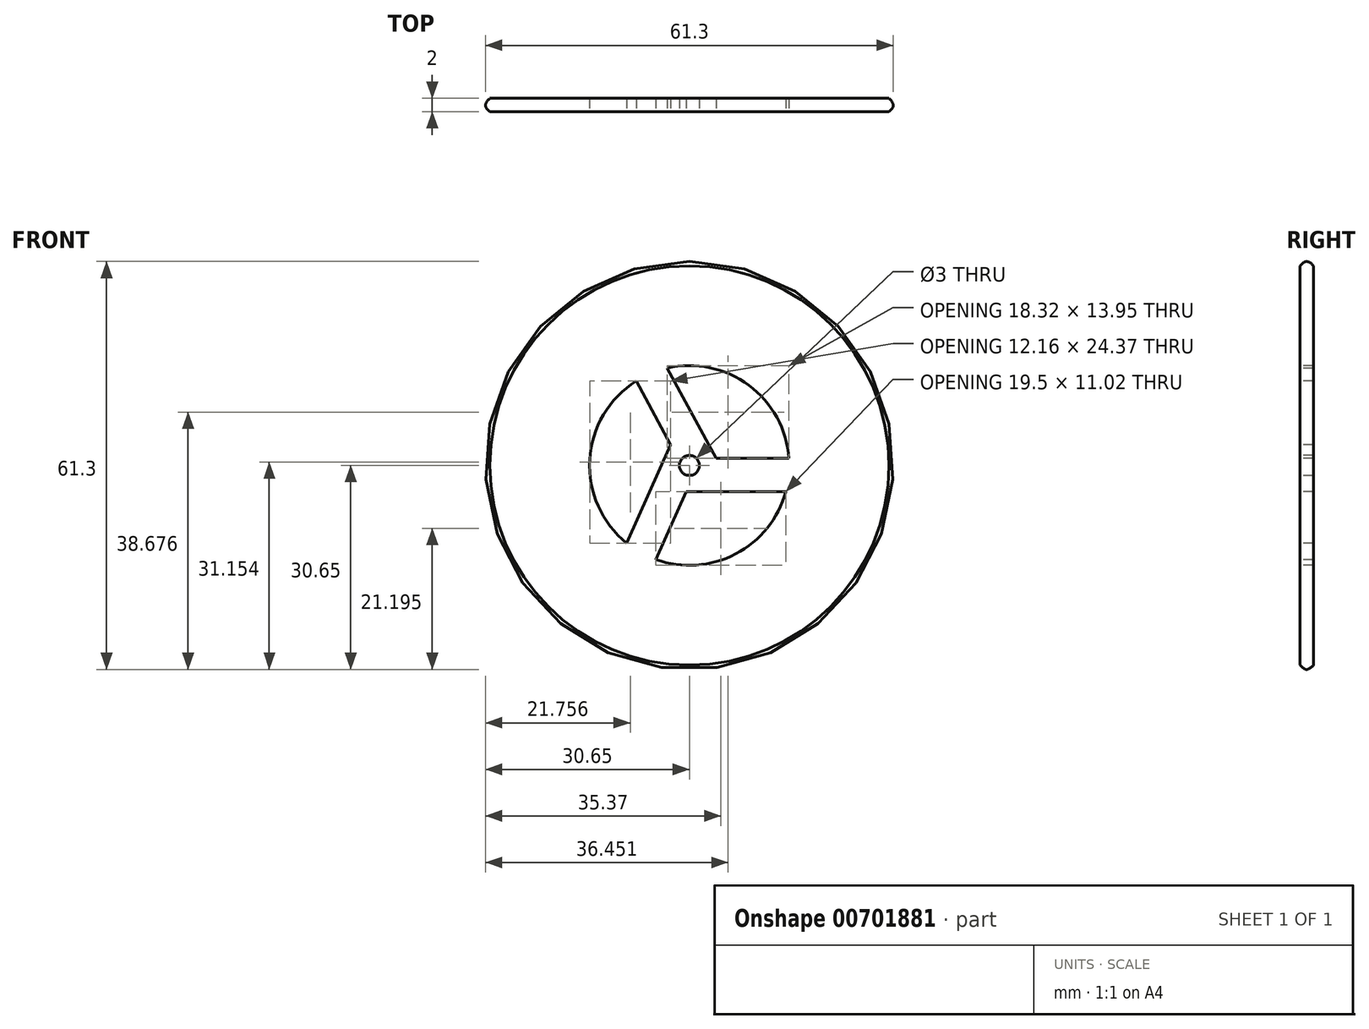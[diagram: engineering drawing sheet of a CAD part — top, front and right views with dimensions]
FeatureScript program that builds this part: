
annotation { "Feature Type Name" : "Feature", "Feature Type Description" : "" }
export const myFeature = defineFeature(function(context is Context, id is Id, definition is map)
    precondition{}
    {
        {
            var Q0;
            Q0=qCreatedBy(makeId("Top.planeOp"),FACE);
            var sketch = newSketch(context, id + "F0", { "sketchPlane" : qUnion([Q0])});
            skLineSegment(sketch, "E0", {"start": v(0, 0) * mm, "end": v(-30, 0) * mm});
            skLineSegment(sketch, "E1", {"start": v(-30, 2) * mm, "end": v(0, 2) * mm});
            skLineSegment(sketch, "E2", {"start": v(0, 2) * mm, "end": v(0, 0) * mm});
            skFitSpline(sketch, "E3", {"points": [v(-30, 2) * mm, v(-30.65, 0.93) * mm, v(-30, 0) * mm], "startDerivative": vector(-2.87, -2.47) * mm, "endDerivative": vector(2.93, -2.74) * mm});
            skSolve(sketch);
        }
        {
            var Q0;
            Q0=makeQuery(id+"F0.imprint","IMPRINT",FACE,{"disambiguationData":[TD([[makeQuery(id+"F0.imprint","IMPRINT",EDGE,{"derivedFrom":sQuery(id+"F0.wireOp",EDGE,"E0")}),-1.0]])]});
            var Q1;
            Q1=sQuery(id+"F0.wireOp",EDGE,"E2");
            revolve(context, id + "F1", {"entities" : qUnion([Q0]), "axis" : qUnion([Q1]), "revolveType" : RevolveType.FULL});
        }
        {
            var Q0;
            Q0=qCreatedBy(makeId("Front.planeOp"),FACE);
            var sketch = newSketch(context, id + "F2", { "sketchPlane" : qUnion([Q0])});
            skCircle(sketch, "E4", {"center": v(0, 0) * mm, "radius": 1.5 * mm});
            skCircle(sketch, "E5", {"center": v(0, 0) * mm, "radius": 3.5 * mm});
            skCircle(sketch, "E6", {"center": v(0, 0) * mm, "radius": 15 * mm});
            skSolve(sketch);
        }
        {
            var Q0;
            Q0=makeQuery(id+"F2.imprint","IMPRINT",FACE,{"disambiguationData":[TD([[makeQuery(id+"F2.imprint","IMPRINT",EDGE,{"derivedFrom":sQuery(id+"F2.wireOp",EDGE,"E4")}),1.0]])]});
            var Q1;
            Q1=makeQuery(id+"F2.imprint","IMPRINT",FACE,{"disambiguationData":[TD([[makeQuery(id+"F2.imprint","IMPRINT",EDGE,{"derivedFrom":sQuery(id+"F2.wireOp",EDGE,"E5")}),-1.0]])]});
            extrude(context, id + "F3", {"entities" : qUnion([Q0, Q1]), "operationType" : NewBodyOperationType.REMOVE, "oppositeDirection" : true, "depth" : 1000 * mm, "offsetDistance" : 25 * mm});
        }
        {
            var Q0;
            Q0=qCreatedBy(makeId("Front.planeOp"),FACE);
            var sketch = newSketch(context, id + "F4", { "sketchPlane" : qUnion([Q0])});
            skLineSegment(sketch, "E7", {"start": v(-9.7, -12.33) * mm, "end": v(-5.13, -14.37) * mm});
            skLineSegment(sketch, "E8", {"start": v(16.52, -3.95) * mm, "end": v(16.52, 1.05) * mm});
            skLineSegment(sketch, "E9", {"start": v(-8.77, 14.1) * mm, "end": v(-4.38, 16.5) * mm});
            skLineSegment(sketch, "E10", {"start": v(-5.13, -14.37) * mm, "end": v(-0.5, -3.95) * mm});
            skLineSegment(sketch, "E11", {"start": v(-0.5, -3.95) * mm, "end": v(16.52, -3.95) * mm});
            skLineSegment(sketch, "E12", {"start": v(-4.38, 16.5) * mm, "end": v(4, 1.05) * mm});
            skLineSegment(sketch, "E13", {"start": v(4, 1.05) * mm, "end": v(16.52, 1.05) * mm});
            skLineSegment(sketch, "E14", {"start": v(-8.77, 14.1) * mm, "end": v(-2.81, 3.13) * mm});
            skLineSegment(sketch, "E15", {"start": v(-9.7, -12.33) * mm, "end": v(-2.81, 3.13) * mm});
            skSolve(sketch);
        }
        {
            var Q0;
            Q0=makeQuery(id+"F4.imprint","IMPRINT",FACE,{"disambiguationData":[TD([[makeQuery(id+"F4.imprint","IMPRINT",EDGE,{"derivedFrom":sQuery(id+"F4.wireOp",EDGE,"E7")}),1.0]])]});
            extrude(context, id + "F5", {"entities" : qUnion([Q0]), "operationType" : NewBodyOperationType.ADD, "oppositeDirection" : true, "depth" : 2 * mm, "offsetDistance" : 25 * mm});
        }
        {
            var Q0;
            Q0=makeQuery(id+"F2.imprint","IMPRINT",FACE,{"disambiguationData":[TD([[makeQuery(id+"F2.imprint","IMPRINT",EDGE,{"derivedFrom":sQuery(id+"F2.wireOp",EDGE,"E4")}),1.0]])]});
            extrude(context, id + "F6", {"entities" : qUnion([Q0]), "operationType" : NewBodyOperationType.REMOVE, "oppositeDirection" : true, "depth" : 10050 * mm, "offsetDistance" : 25 * mm});
        }
    });
